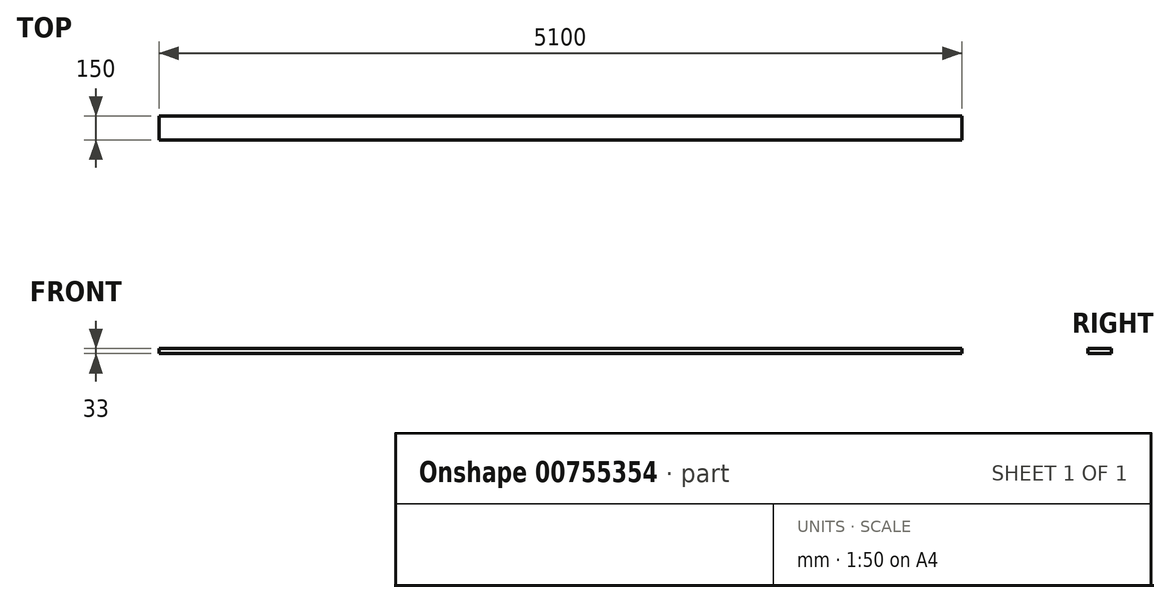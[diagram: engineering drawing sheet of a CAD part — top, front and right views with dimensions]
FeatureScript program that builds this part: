
annotation { "Feature Type Name" : "Feature", "Feature Type Description" : "" }
export const myFeature = defineFeature(function(context is Context, id is Id, definition is map)
    precondition{}
    {
        {
            var Q0;
            Q0=qCreatedBy(makeId("Right.planeOp"),FACE);
            var sketch = newSketch(context, id + "F0", { "sketchPlane" : qUnion([Q0])});
            skLineSegment(sketch, "E0.bottom", {"start": v(75, 16.5) * mm, "end": v(-75, 16.5) * mm});
            skLineSegment(sketch, "E0.top", {"start": v(75, -16.5) * mm, "end": v(-75, -16.5) * mm});
            skLineSegment(sketch, "E0.left", {"start": v(75, 16.5) * mm, "end": v(75, -16.5) * mm});
            skLineSegment(sketch, "E0.right", {"start": v(-75, 16.5) * mm, "end": v(-75, -16.5) * mm});
            skPoint(sketch, "E0.middle", {"position": v(0, 0) * mm});
            skSolve(sketch);
        }
        {
            var Q0;
            Q0 = qSketchRegion(id + "F0", true);
            extrude(context, id + "F1", {"entities" : qUnion([Q0]), "endBound" : BoundingType.SYMMETRIC, "depth" : 5100 * mm, "offsetDistance" : 25 * mm});
        }
    });
